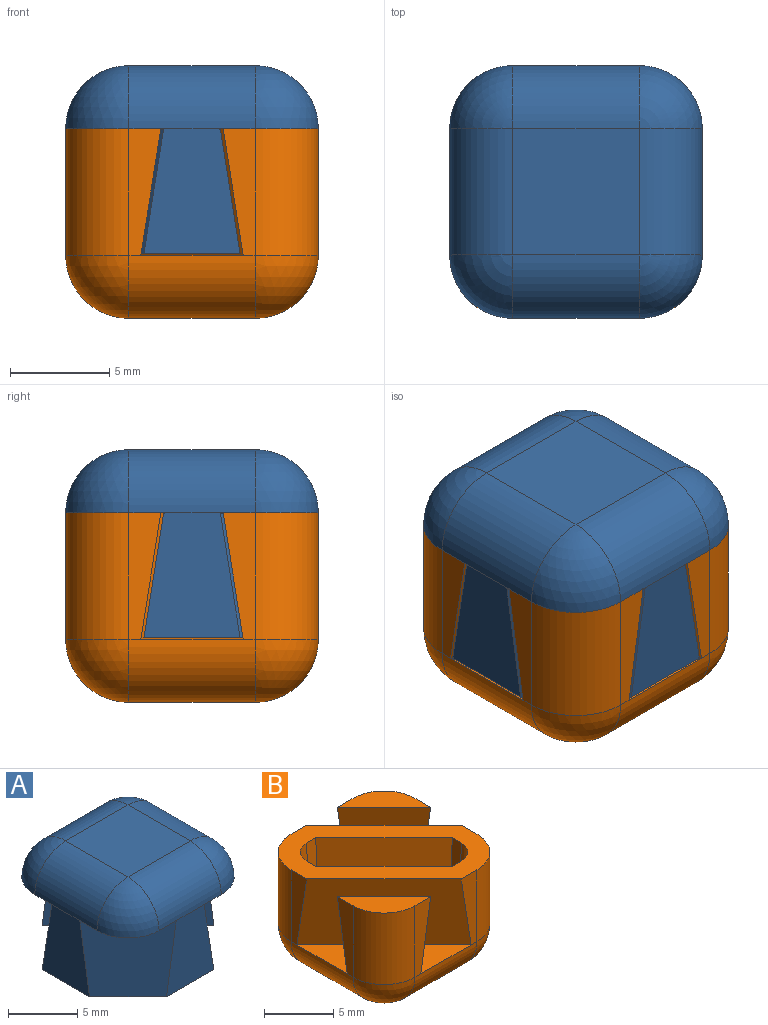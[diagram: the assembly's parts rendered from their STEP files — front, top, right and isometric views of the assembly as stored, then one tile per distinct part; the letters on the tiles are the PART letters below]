
ASSEMBLY  parts=2 mates=1
PART A: 30 faces, bbox 12.7x12.7x9.4 mm
  f0: plane 6.25x4.83mm, normal (1,0,0), area 24mm2, adj f10,f16,f17,f19,f20,f29
  f1: plane 6.25x4.83mm, normal (0,1,0), area 24mm2, adj f9,f16,f17,f19,f20,f28
  f2: plane 6.25x4.83mm, normal (-1,0,0), area 24mm2, adj f13,f21,f22,f24,f25,f27
  f3: plane 6.25x4.83mm, normal (0,-1,0), area 24mm2, adj f14,f21,f22,f24,f25,f26
  f4: plane 6.35x6.35mm, normal (0,0,1), area 40.3mm2, adj f9,f10,f13,f14
  f5: plane 4.78x4.78mm, normal (0,0,-1), area 9.3mm2, adj f13,f14,f15,f23
  f6: plane 12.7x12.7mm, normal (0,0,-1), area 94.3mm2, adj f9,f10,f11,f12,f13,f14,f17,f22
  f7: plane 4.78x4.78mm, normal (0,0,-1), area 9.3mm2, adj f8,f9,f10,f18
  f8: sphere r=3.17mm, area 15.8mm2, adj f7,f9,f10
  f9: cylinder r=3.17mm len=6.35mm, axis (-1,0,0), area 31.7mm2, adj f1,f4,f6,f7,f8,f11
  f10: cylinder r=3.17mm len=6.35mm, axis (0,1,0), area 31.7mm2, adj f0,f4,f6,f7,f8,f12
  f11: sphere r=3.17mm, area 15.8mm2, adj f6,f9,f13
  f12: sphere r=3.17mm, area 15.8mm2, adj f6,f10,f14
  f13: cylinder r=3.17mm len=6.35mm, axis (0,-1,0), area 31.7mm2, adj f2,f4,f5,f6,f11,f15
  f14: cylinder r=3.17mm len=6.35mm, axis (1,0,0), area 31.7mm2, adj f3,f4,f5,f6,f12,f15
  f15: sphere r=3.17mm, area 15.8mm2, adj f5,f13,f14
  f16: plane 8.77x8.77mm, normal (-0.7,-0.7,0.11), area 73.5mm2, adj f0,f1,f17,f20
  f17: plane 7.92x7.92mm, normal (-0.08,-0.08,-0.99), area 1.1mm2, adj f0,f1,f6,f16
  f18: plane 4.85x4.85mm, normal (0.08,0.08,-0.99), area 0.7mm2, adj f7,f19,f28,f29
  f19: plane 6.24x4.92mm, normal (0.7,0.7,0.11), area 39.3mm2, adj f0,f1,f18,f20,f28,f29
  f20: plane 8.77x8.77mm, normal (0,0,-1), area 30.7mm2, adj f0,f1,f16,f19
  f21: plane 8.77x8.77mm, normal (0.7,0.7,0.11), area 73.5mm2, adj f2,f3,f22,f24
  f22: plane 7.92x7.92mm, normal (0.08,0.08,-0.99), area 1.1mm2, adj f2,f3,f6,f21
  f23: plane 4.85x4.85mm, normal (-0.08,-0.08,-0.99), area 0.7mm2, adj f5,f25,f26,f27
  f24: plane 8.77x8.77mm, normal (0,0,-1), area 30.7mm2, adj f2,f3,f21,f25
  f25: plane 6.24x4.92mm, normal (-0.7,-0.7,0.11), area 39.3mm2, adj f2,f3,f23,f24,f26,f27
  f26: plane 0.14x0.07mm, normal (-0.16,0,-0.99), area 0mm2, adj f3,f23,f25
  f27: plane 0.14x0.07mm, normal (0,-0.16,-0.99), area 0mm2, adj f2,f23,f25
  f28: plane 0.14x0.07mm, normal (0.16,0,-0.99), area 0mm2, adj f1,f18,f19
  f29: plane 0.14x0.07mm, normal (0,0.16,-0.99), area 0mm2, adj f0,f18,f19
PART B: 39 faces, bbox 12.7x12.7x9.5 mm
  f0: plane 6.35x1.61mm, normal (0,1,0), area 7mm2, adj f4,f12,f16,f22
  f1: plane 6.35x1.61mm, normal (1,0,0), area 7mm2, adj f5,f14,f18,f26
  f2: plane 6.35x1.61mm, normal (-1,0,0), area 7mm2, adj f5,f13,f21,f25
  f3: plane 6.35x1.61mm, normal (0,-1,0), area 7mm2, adj f10,f15,f20,f29
  f4: plane 4.78x4.78mm, normal (0,0,1), area 9.3mm2, adj f0,f6,f12,f16
  f5: plane 12.7x12.7mm, normal (0,0,1), area 53.5mm2, adj f1,f2,f7,f11,f13,f14,f18,f21
  f6: plane 6.35x1.61mm, normal (1,0,0), area 7mm2, adj f4,f12,f16,f26
  f7: plane 6.35x1.61mm, normal (0,1,0), area 7mm2, adj f5,f13,f18,f22
  f8: plane 6.35x1.61mm, normal (-1,0,0), area 7mm2, adj f10,f15,f20,f25
  f9: plane 6.35x6.35mm, normal (0,0,-1), area 40.3mm2, adj f22,f25,f26,f29
  f10: plane 4.78x4.78mm, normal (0,0,1), area 9.3mm2, adj f3,f8,f15,f20
  f11: plane 6.35x1.61mm, normal (0,-1,0), area 7mm2, adj f5,f14,f21,f29
  f12: cylinder r=3.17mm len=6.35mm, axis (0,0,1), area 31.7mm2, adj f0,f4,f6,f24
  f13: cylinder r=3.17mm len=6.35mm, axis (0,0,-1), area 31.7mm2, adj f2,f5,f7,f23
  f14: cylinder r=3.17mm len=6.35mm, axis (0,0,-1), area 31.7mm2, adj f1,f5,f11,f28
  f15: cylinder r=3.17mm len=6.35mm, axis (0,0,1), area 31.7mm2, adj f3,f8,f10,f27
  f16: plane 6.35x4.78mm, normal (-0.7,-0.7,-0.11), area 38.7mm2, adj f0,f4,f6,f17
  f17: plane 8.92x8.92mm, normal (0,0,1), area 32.7mm2, adj f16,f18,f22,f26
  f18: plane 8.92x8.92mm, normal (0.7,0.7,-0.11), area 76.1mm2, adj f1,f5,f7,f17
  f19: plane 8.92x8.92mm, normal (0,0,1), area 32.7mm2, adj f20,f21,f25,f29
  f20: plane 6.35x4.78mm, normal (0.7,0.7,-0.11), area 38.7mm2, adj f3,f8,f10,f19
  f21: plane 8.92x8.92mm, normal (-0.7,-0.7,-0.11), area 76.1mm2, adj f2,f5,f11,f19
  f22: cylinder r=3.17mm len=6.35mm, axis (1,0,0), area 31.7mm2, adj f0,f7,f9,f17,f23,f24
  f23: sphere r=3.17mm, area 15.8mm2, adj f13,f22,f25
  f24: sphere r=3.17mm, area 15.8mm2, adj f12,f22,f26
  f25: cylinder r=3.17mm len=6.35mm, axis (0,1,0), area 31.7mm2, adj f2,f8,f9,f19,f23,f27
  f26: cylinder r=3.17mm len=6.35mm, axis (0,-1,0), area 31.7mm2, adj f1,f6,f9,f17,f24,f28
  f27: sphere r=3.17mm, area 15.8mm2, adj f15,f25,f29
  f28: sphere r=3.17mm, area 15.8mm2, adj f14,f26,f29
  f29: cylinder r=3.17mm len=6.35mm, axis (-1,0,0), area 31.7mm2, adj f3,f9,f11,f19,f27,f28
  f30: plane 8.86x8.86mm, normal (0,0,1), area 31.7mm2, adj f31,f32,f33,f34,f35,f36,f37,f38
  f31: plane 6.35x0.95mm, normal (1,0,0.05), area 5.6mm2, adj f5,f30,f32,f38
  f32: plane 7.13x7.13mm, normal (0.71,0.71,0.05), area 62mm2, adj f5,f30,f31,f33
  f33: plane 6.35x0.95mm, normal (0,1,0.05), area 5.6mm2, adj f5,f30,f32,f34
  f34: cone r=1.59mm half-angle=3deg, axis (0,0,1), area 14.2mm2, adj f5,f30,f33,f35
  f35: plane 6.35x0.95mm, normal (-1,0,0.05), area 5.6mm2, adj f5,f30,f34,f36
  f36: plane 7.13x7.13mm, normal (-0.71,-0.71,0.05), area 62mm2, adj f5,f30,f35,f37
  f37: plane 6.35x0.95mm, normal (0,-1,0.05), area 5.6mm2, adj f5,f30,f36,f38
  f38: cone r=1.59mm half-angle=3deg, axis (0,0,1), area 14.2mm2, adj f5,f30,f31,f37
PLACE A t=(25.4,0,0)mm
PLACE B at identity
MATE fastened A.f6 <-> B.f5  axis (0,0,1) through (-6.97,0,3.26)mm
